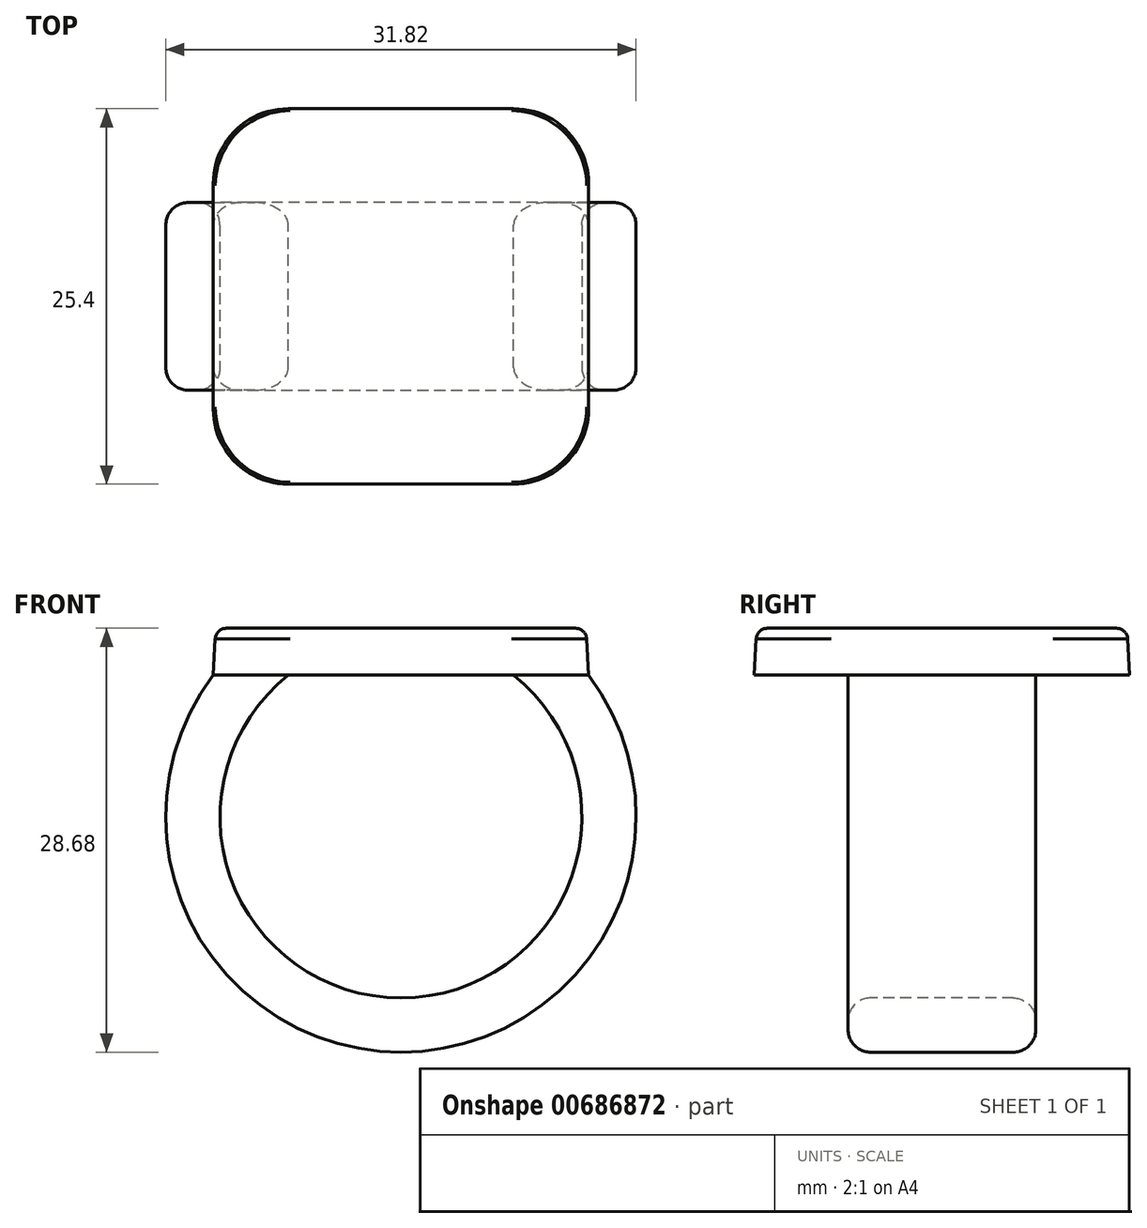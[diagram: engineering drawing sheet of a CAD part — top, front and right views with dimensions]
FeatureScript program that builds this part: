
annotation { "Feature Type Name" : "Feature", "Feature Type Description" : "" }
export const myFeature = defineFeature(function(context is Context, id is Id, definition is map)
    precondition{}
    {
        {
            var Q0;
            Q0=qCreatedBy(makeId("Top.planeOp"),FACE);
            var sketch = newSketch(context, id + "F0", { "sketchPlane" : qUnion([Q0])});
            skLineSegment(sketch, "E0.bottom", {"start": v(12.7, 12.7) * mm, "end": v(-12.7, 12.7) * mm});
            skLineSegment(sketch, "E0.top", {"start": v(12.7, -12.7) * mm, "end": v(-12.7, -12.7) * mm});
            skLineSegment(sketch, "E0.left", {"start": v(12.7, 12.7) * mm, "end": v(12.7, -12.7) * mm});
            skLineSegment(sketch, "E0.right", {"start": v(-12.7, 12.7) * mm, "end": v(-12.7, -12.7) * mm});
            skPoint(sketch, "E0.middle", {"position": v(0, 0) * mm});
            skSolve(sketch);
        }
        {
            var Q0;
            Q0=makeQuery(id+"F0.imprint","IMPRINT",FACE,{"disambiguationData":[TD([[makeQuery(id+"F0.imprint","IMPRINT",EDGE,{"derivedFrom":sQuery(id+"F0.wireOp",EDGE,"E0.bottom")}),1.0]])]});
            extrude(context, id + "F1", {"entities" : qUnion([Q0]), "depth" : 3.17 * mm, "offsetDistance" : 25.4 * mm, "hasDraft" : true, "draftAngle" : 3 * degree, "draftPullDirection" : true});
        }
        {
            var Q0;
            Q0=qCreatedBy(makeId("Front.planeOp"),FACE);
            var sketch = newSketch(context, id + "F2", { "sketchPlane" : qUnion([Q0])});
            skArc(sketch, "E1", {"start": v(-10.16, 0) * mm, "mid": v(0, -23.56) * mm, "end": v(10.16, 0) * mm});
            skSolve(sketch);
        }
        {
            var Q0;
            Q0=makeQuery(id+"F1.opExtrude","CAP_FACE",FACE,{"disambiguationData":[OSD([sQuery(id+"F0.wireOp",EDGE,"E0.bottom"),sQuery(id+"F0.wireOp",EDGE,"E0.top"),sQuery(id+"F0.wireOp",EDGE,"E0.left"),sQuery(id+"F0.wireOp",EDGE,"E0.right")])],"isStart":true});
            var sketch = newSketch(context, id + "F3", { "sketchPlane" : qUnion([Q0])});
            skLineSegment(sketch, "E2.bottom", {"start": v(-7.62, 6.35) * mm, "end": v(-12.7, 6.35) * mm});
            skLineSegment(sketch, "E2.top", {"start": v(-7.62, -6.35) * mm, "end": v(-12.7, -6.35) * mm});
            skLineSegment(sketch, "E2.left", {"start": v(-7.62, 6.35) * mm, "end": v(-7.62, -6.35) * mm});
            skLineSegment(sketch, "E2.right", {"start": v(-12.7, 6.35) * mm, "end": v(-12.7, -6.35) * mm});
            skPoint(sketch, "E2.middle", {"position": v(-10.16, 0) * mm});
            skSolve(sketch);
        }
        {
            var Q0;
            Q0 = qSketchRegion(id + "F3", true);
            var Q1;
            Q1 = qConstructionFilter(qBodyType(qCreatedBy(id + "F2" ,EDGE), BodyType.WIRE), ConstructionObject.NO);
            sweep(context, id + "F4", {"operationType" : NewBodyOperationType.ADD, "profiles" : qUnion([Q0]), "path" : qUnion([Q1])});
        }
        {
            var Q0;
            Q0=qCreatedBy(makeId("Front.planeOp"),FACE);
            var sketch = newSketch(context, id + "F5", { "sketchPlane" : qUnion([Q0])});
            skArc(sketch, "E3.0", {"start": v(10.01, -2.54) * mm, "mid": v(8.9, -1.18) * mm, "end": v(7.62, 0) * mm});
            skLineSegment(sketch, "E3.1", {"start": v(10.01, -2.54) * mm, "end": v(10.16, 0) * mm});
            skLineSegment(sketch, "E3.2", {"start": v(10.16, 0) * mm, "end": v(7.62, 0) * mm});
            skPoint(sketch, "E4.orphan", {"position": v(-12.7, 0) * mm});
            skPoint(sketch, "E5.orphan", {"position": v(12.7, 0) * mm});
            skPoint(sketch, "E6.orphan", {"position": v(-7.62, 0) * mm});
            skSolve(sketch);
        }
        {
            var Q0;
            Q0=makeQuery(id+"F5.imprint","IMPRINT",FACE,{"disambiguationData":[TD([[makeQuery(id+"F5.imprint","IMPRINT",EDGE,{"derivedFrom":sQuery(id+"F5.wireOp",EDGE,"E3.0")}),-1.0]])]});
            var Q1;
            Q1=makeQuery(id+"F4.opSweep","SWEPT_FACE",FACE,{"disambiguationData":[OSD([sQuery(id+"F2.wireOp",EDGE,"E1"),sQuery(id+"F3.wireOp",EDGE,"E2.bottom")])]});
            var Q2;
            Q2=makeQuery(id+"F4.opSweep","SWEPT_FACE",FACE,{"disambiguationData":[OSD([sQuery(id+"F2.wireOp",EDGE,"E1"),sQuery(id+"F3.wireOp",EDGE,"E2.top")])]});
            extrude(context, id + "F6", {"entities" : qUnion([Q0]), "operationType" : NewBodyOperationType.ADD, "endBound" : BoundingType.UP_TO_SURFACE, "depth" : 25.4 * mm, "endBoundEntityFace" : qUnion([Q1]), "offsetDistance" : 25.4 * mm, "hasSecondDirection" : true, "secondDirectionBound" : SecondDirectionBoundingType.UP_TO_SURFACE, "secondDirectionOppositeDirection" : true, "secondDirectionDepth" : 25.4 * mm, "secondDirectionBoundEntityFace" : qUnion([Q2])});
        }
        {
            var Q0;
            Q0=makeQuery(id+"F1.opExtrude","SWEPT_EDGE",EDGE,{"disambiguationData":[OSD([sQuery(id+"F0.wireOp",EDGE,"E0.top"),sQuery(id+"F0.wireOp",EDGE,"E0.left")])]});
            var Q1;
            Q1=makeQuery(id+"F1.opExtrude","SWEPT_EDGE",EDGE,{"disambiguationData":[OSD([sQuery(id+"F0.wireOp",EDGE,"E0.top"),sQuery(id+"F0.wireOp",EDGE,"E0.right")])]});
            var Q2;
            Q2=makeQuery(id+"F1.opExtrude","SWEPT_EDGE",EDGE,{"disambiguationData":[OSD([sQuery(id+"F0.wireOp",EDGE,"E0.bottom"),sQuery(id+"F0.wireOp",EDGE,"E0.right")])]});
            var Q3;
            Q3=makeQuery(id+"F1.opExtrude","SWEPT_EDGE",EDGE,{"disambiguationData":[OSD([sQuery(id+"F0.wireOp",EDGE,"E0.bottom"),sQuery(id+"F0.wireOp",EDGE,"E0.left")])]});
            fillet(context, id + "F7", {"entities" : qUnion([Q0, Q1, Q2, Q3]), "radius" : 5.08 * mm, "tangentPropagation" : true, "allowEdgeOverflow" : false});
        }
        {
            var Q0;
            Q0=makeQuery(id+"F4.opSweep","SWEPT_EDGE",EDGE,{"disambiguationData":[OSD([sQuery(id+"F0.wireOp",EDGE,"E0.right"),sQuery(id+"F2.wireOp",EDGE,"E1"),sQuery(id+"F3.wireOp",EDGE,"E2.top"),sQuery(id+"F3.wireOp",EDGE,"E2.right")])]});
            var Q1;
            Q1=makeQuery(id+"F4.opSweep","SWEPT_EDGE",EDGE,{"disambiguationData":[OSD([sQuery(id+"F0.wireOp",EDGE,"E0.right"),sQuery(id+"F2.wireOp",EDGE,"E1"),sQuery(id+"F3.wireOp",EDGE,"E2.bottom"),sQuery(id+"F3.wireOp",EDGE,"E2.right")])]});
            var Q2;
            {var subQ0=sQuery(id+"F3.wireOp",EDGE,"E2.top");var subQ1=sQuery(id+"F2.wireOp",EDGE,"E1");Q2=makeQuery(id+"F6.boolean.opBoolean","MERGE",EDGE,{"derivedFrom":[makeQuery(id+"F4.opSweep","SWEPT_EDGE",EDGE,{"disambiguationData":[OSD([subQ1,subQ0,sQuery(id+"F3.wireOp",EDGE,"E2.left")])]}),makeQuery(id+"F6.opExtrude","TWEAK_EDGE",EDGE,{"derivedFrom":[makeQuery(id+"F4.opSweep","SWEPT_FACE",FACE,{"disambiguationData":[OSD([subQ1,subQ0])]}),makeQuery(id+"F5.imprint","IMPRINT",EDGE,{"derivedFrom":sQuery(id+"F5.wireOp",EDGE,"E3.0")})]})]});}
            var Q3;
            {var subQ0=sQuery(id+"F3.wireOp",EDGE,"E2.bottom");var subQ1=sQuery(id+"F2.wireOp",EDGE,"E1");Q3=makeQuery(id+"F6.boolean.opBoolean","MERGE",EDGE,{"derivedFrom":[makeQuery(id+"F4.opSweep","SWEPT_EDGE",EDGE,{"disambiguationData":[OSD([subQ1,subQ0,sQuery(id+"F3.wireOp",EDGE,"E2.left")])]}),makeQuery(id+"F6.opExtrude","TWEAK_EDGE",EDGE,{"derivedFrom":[makeQuery(id+"F4.opSweep","SWEPT_FACE",FACE,{"disambiguationData":[OSD([subQ1,subQ0])]}),makeQuery(id+"F5.imprint","IMPRINT",EDGE,{"derivedFrom":sQuery(id+"F5.wireOp",EDGE,"E3.0")})]})]});}
            fillet(context, id + "F8", {"entities" : qUnion([Q0, Q1, Q2, Q3]), "radius" : 1.52 * mm, "tangentPropagation" : true, "allowEdgeOverflow" : false});
        }
        {
            var Q0;
            Q0=makeQuery(id+"F1.opExtrude","CAP_FACE",FACE,{"disambiguationData":[OSD([sQuery(id+"F0.wireOp",EDGE,"E0.bottom"),sQuery(id+"F0.wireOp",EDGE,"E0.top"),sQuery(id+"F0.wireOp",EDGE,"E0.left"),sQuery(id+"F0.wireOp",EDGE,"E0.right")])],"isStart":false});
            fillet(context, id + "F9", {"entities" : qUnion([Q0]), "radius" : 0.76 * mm, "tangentPropagation" : true, "allowEdgeOverflow" : false});
        }
    });
